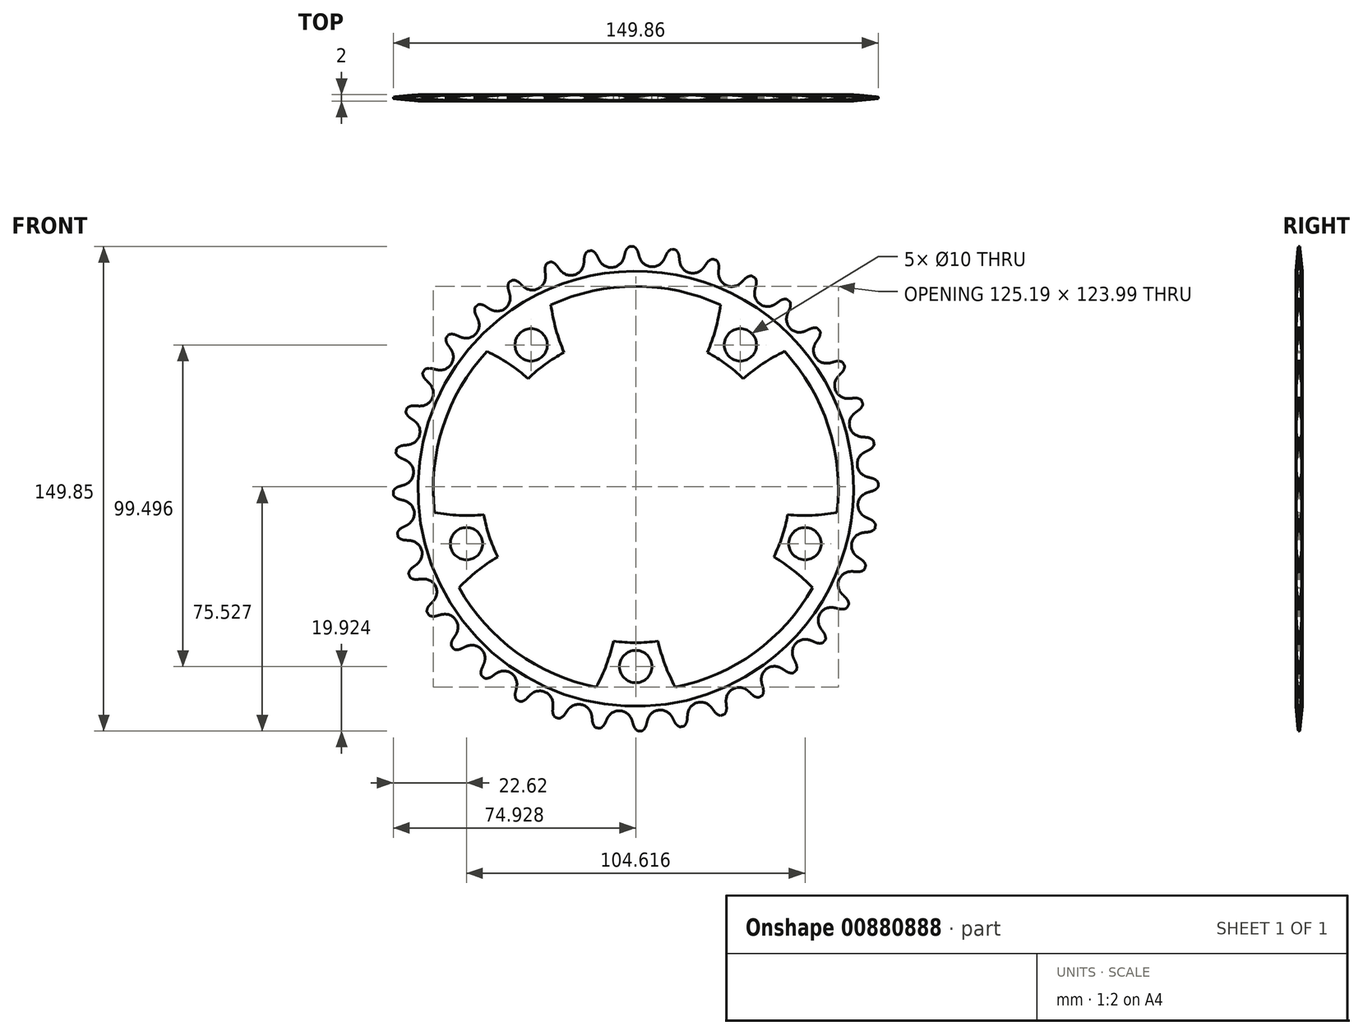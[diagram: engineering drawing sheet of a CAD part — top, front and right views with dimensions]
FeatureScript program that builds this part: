
annotation { "Feature Type Name" : "Feature", "Feature Type Description" : "" }
export const myFeature = defineFeature(function(context is Context, id is Id, definition is map)
    precondition{}
    {
        {
            var Q0;
            Q0=qCreatedBy(makeId("Front.planeOp"),FACE);
            var sketch = newSketch(context, id + "F0", { "sketchPlane" : qUnion([Q0])});
            skArc(sketch, "E0", {"start": v(-38.32, -39.45) * mm, "mid": v(52.3, 17) * mm, "end": v(-54.2, 9.39) * mm, "construction": true});
            skCircle(sketch, "E1", {"center": v(0, 55) * mm, "radius": 5 * mm});
            skCircle(sketch, "E2.1.0", {"center": v(-52.3, 17) * mm, "radius": 5 * mm});
            skCircle(sketch, "E2.2.0", {"center": v(-32.33, -44.5) * mm, "radius": 5 * mm});
            skCircle(sketch, "E2.3.0", {"center": v(32.33, -44.5) * mm, "radius": 5 * mm});
            skCircle(sketch, "E2.4.0", {"center": v(52.3, 17) * mm, "radius": 5 * mm});
            skLineSegment(sketch, "E3", {"start": v(0, 55) * mm, "end": v(0, 7.81) * mm, "construction": true});
            skLineSegment(sketch, "E4.2.3.0", {"start": v(21.9, -38.96) * mm, "end": v(21.9, -38.96) * mm});
            skLineSegment(sketch, "E4.4.3.0", {"start": v(32.98, -30.9) * mm, "end": v(32.98, -30.9) * mm});
            skLineSegment(sketch, "E5", {"start": v(41.79, 25.51) * mm, "end": v(41.79, 25.51) * mm});
            skArc(sketch, "E6", {"start": v(46.92, 8.04) * mm, "mid": v(45.27, 14.7) * mm, "end": v(42.68, 21.07) * mm});
            skArc(sketch, "E7", {"start": v(22.14, -42.14) * mm, "mid": v(27.98, -38.5) * mm, "end": v(33.23, -34.08) * mm});
            skArc(sketch, "E8", {"start": v(-33.23, -34.08) * mm, "mid": v(-27.98, -38.5) * mm, "end": v(-22.14, -42.14) * mm});
            skArc(sketch, "E9", {"start": v(-42.68, 21.07) * mm, "mid": v(-45.27, 14.7) * mm, "end": v(-46.92, 8.04) * mm});
            skArc(sketch, "E10.1.0", {"start": v(6.85, 47.1) * mm, "mid": v(0, 47.6) * mm, "end": v(-6.85, 47.1) * mm});
            skCircle(sketch, "E11", {"center": v(0, 0) * mm, "radius": 74.93 * mm});
            skPoint(sketch, "E12.orphan", {"position": v(26.2, -56.86) * mm});
            skPoint(sketch, "E13.orphan", {"position": v(45.98, -42.48) * mm});
            skPoint(sketch, "E14.orphan", {"position": v(-26.2, -56.86) * mm});
            skPoint(sketch, "E15.orphan", {"position": v(-45.98, -42.48) * mm});
            skPoint(sketch, "E16.orphan", {"position": v(-62.17, 7.34) * mm});
            skPoint(sketch, "E17.orphan", {"position": v(-54.61, 30.6) * mm});
            skPoint(sketch, "E18.orphan", {"position": v(-12.23, 61.4) * mm});
            skPoint(sketch, "E19.orphan", {"position": v(12.23, 61.4) * mm});
            skPoint(sketch, "E20.orphan", {"position": v(62.17, 7.34) * mm});
            skPoint(sketch, "E21.orphan", {"position": v(42.68, 21.07) * mm});
            skPoint(sketch, "E22.orphan", {"position": v(-22.14, -42.14) * mm});
            skPoint(sketch, "E23.orphan", {"position": v(-33.23, -34.08) * mm});
            skPoint(sketch, "E24.orphan", {"position": v(-46.92, 8.04) * mm});
            skPoint(sketch, "E25.MirrorCS.start.orphan", {"position": v(6.85, 47.1) * mm});
            skPoint(sketch, "E26.orphan", {"position": v(-6.85, 47.1) * mm});
            skArc(sketch, "E27", {"start": v(-54.61, 30.6) * mm, "mid": v(-48.97, 25.43) * mm, "end": v(-42.68, 21.07) * mm});
            skLineSegment(sketch, "E28.MirrorCS", {"start": v(-62.42, 10.52) * mm, "end": v(-62.42, 10.52) * mm});
            skArc(sketch, "E29.1.0", {"start": v(-45.98, -42.48) * mm, "mid": v(-39.32, -38.72) * mm, "end": v(-33.23, -34.08) * mm});
            skArc(sketch, "E29.1.1", {"start": v(-26.2, -56.86) * mm, "mid": v(-24.67, -49.36) * mm, "end": v(-22.14, -42.14) * mm});
            skArc(sketch, "E29.2.0", {"start": v(26.2, -56.86) * mm, "mid": v(24.67, -49.36) * mm, "end": v(22.14, -42.14) * mm});
            skLineSegment(sketch, "E29.2.1", {"start": v(45.73, -39.3) * mm, "end": v(45.73, -39.3) * mm});
            skArc(sketch, "E29.3.0", {"start": v(62.17, 7.34) * mm, "mid": v(54.57, 8.21) * mm, "end": v(46.92, 8.04) * mm});
            skArc(sketch, "E29.3.1", {"start": v(54.61, 30.6) * mm, "mid": v(48.97, 25.43) * mm, "end": v(42.68, 21.07) * mm});
            skArc(sketch, "E29.4.0", {"start": v(12.23, 61.4) * mm, "mid": v(9.05, 54.43) * mm, "end": v(6.85, 47.1) * mm});
            skArc(sketch, "E29.4.1", {"start": v(-12.23, 61.4) * mm, "mid": v(-9.05, 54.43) * mm, "end": v(-6.85, 47.1) * mm});
            skArc(sketch, "E30", {"start": v(-12.23, 61.4) * mm, "mid": v(-36.8, 50.64) * mm, "end": v(-54.61, 30.6) * mm});
            skArc(sketch, "E31", {"start": v(54.61, 30.6) * mm, "mid": v(36.8, 50.64) * mm, "end": v(12.23, 61.4) * mm});
            skArc(sketch, "E32", {"start": v(45.98, -42.48) * mm, "mid": v(39.32, -38.72) * mm, "end": v(33.23, -34.08) * mm});
            skArc(sketch, "E33", {"start": v(45.98, -42.48) * mm, "mid": v(59.54, -19.34) * mm, "end": v(62.17, 7.34) * mm});
            skArc(sketch, "E34", {"start": v(-62.17, 7.34) * mm, "mid": v(-59.54, -19.34) * mm, "end": v(-45.98, -42.48) * mm});
            skArc(sketch, "E35", {"start": v(-62.17, 7.34) * mm, "mid": v(-54.57, 8.21) * mm, "end": v(-46.92, 8.04) * mm});
            skArc(sketch, "E36", {"start": v(-26.2, -56.86) * mm, "mid": v(0, -62.6) * mm, "end": v(26.2, -56.86) * mm});
            skSolve(sketch);
        }
        {
            var Q0;
            Q0=qCreatedBy(makeId("Front.planeOp"),FACE);
            cPlane(context, id + "F1", {"entities" : qUnion([Q0]), "cplaneType" : CPlaneType.OFFSET, "offset" : 25.4 * mm, "width" : 152.4 * mm, "height" : 152.4 * mm});
        }
        {
            var Q0;
            Q0=qCreatedBy(id+"F1.planeOp",FACE);
            var sketch = newSketch(context, id + "F2", { "sketchPlane" : qUnion([Q0])});
            skCircle(sketch, "E37", {"center": v(0, 0) * mm, "radius": 72.86 * mm, "construction": true});
            skLineSegment(sketch, "E38", {"start": v(0, 0) * mm, "end": v(0, 72.86) * mm, "construction": true});
            skLineSegment(sketch, "E39", {"start": v(0, 72.86) * mm, "end": v(8.72, 72.86) * mm, "construction": true});
            skLineSegment(sketch, "E40", {"start": v(0, 72.86) * mm, "end": v(0.93, 73.55) * mm, "construction": true});
            skLineSegment(sketch, "E41", {"start": v(0.93, 73.55) * mm, "end": v(-3.94, 71.76) * mm, "construction": true});
            skLineSegment(sketch, "E42", {"start": v(-123.38, 117.03) * mm, "end": v(-123.38, 117.03) * mm});
            skLineSegment(sketch, "E43", {"start": v(-6.56, 75) * mm, "end": v(0, 0) * mm, "construction": true});
            skArc(sketch, "E44", {"start": v(-6.56, 75) * mm, "mid": v(-9.6, 69.52) * mm, "end": v(-4.4, 73) * mm, "construction": true});
            skArc(sketch, "E45", {"start": v(-4.4, 73) * mm, "mid": v(-5.24, 74.26) * mm, "end": v(-6.56, 75) * mm});
            skArc(sketch, "E46", {"start": v(-3.94, 71.76) * mm, "mid": v(-3.63, 71.08) * mm, "end": v(-3.23, 70.45) * mm});
            skLineSegment(sketch, "E47", {"start": v(-122.67, 115.72) * mm, "end": v(-122.67, 115.72) * mm});
            skLineSegment(sketch, "E48", {"start": v(-4.4, 73) * mm, "end": v(-5.3, 75.44) * mm, "construction": true});
            skLineSegment(sketch, "E49", {"start": v(-3.94, 71.76) * mm, "end": v(-4.4, 73) * mm});
            skArc(sketch, "E50.MirrorCS", {"start": v(4.4, 73) * mm, "mid": v(5.24, 74.26) * mm, "end": v(6.56, 75) * mm});
            skLineSegment(sketch, "E51.MirrorCS", {"start": v(3.94, 71.76) * mm, "end": v(4.4, 73) * mm});
            skArc(sketch, "E52.MirrorCS", {"start": v(3.94, 71.76) * mm, "mid": v(3.63, 71.08) * mm, "end": v(3.23, 70.45) * mm});
            skArc(sketch, "E53", {"start": v(-3.23, 70.45) * mm, "mid": v(5.5, 76.02) * mm, "end": v(-3.94, 71.76) * mm, "construction": true});
            skLineSegment(sketch, "E54", {"start": v(-116.21, 115.72) * mm, "end": v(-116.21, 115.72) * mm});
            skArc(sketch, "E55", {"start": v(-3.23, 70.45) * mm, "mid": v(0, 68.83) * mm, "end": v(3.23, 70.45) * mm});
            skArc(sketch, "E56", {"start": v(3.23, 70.45) * mm, "mid": v(0, 76.89) * mm, "end": v(-3.23, 70.45) * mm, "construction": true});
            skArc(sketch, "E57.1.0", {"start": v(-17, 71.13) * mm, "mid": v(-18.05, 72.22) * mm, "end": v(-19.48, 72.71) * mm});
            skLineSegment(sketch, "E57.1.1", {"start": v(-16.34, 69.98) * mm, "end": v(-17, 71.13) * mm});
            skArc(sketch, "E57.1.2", {"start": v(-16.34, 69.98) * mm, "mid": v(-15.92, 69.37) * mm, "end": v(-15.42, 68.82) * mm});
            skArc(sketch, "E57.1.3", {"start": v(-15.42, 68.82) * mm, "mid": v(-11.95, 67.79) * mm, "end": v(-9.05, 69.94) * mm});
            skArc(sketch, "E57.1.4", {"start": v(-8.58, 71.35) * mm, "mid": v(-8.77, 70.63) * mm, "end": v(-9.05, 69.94) * mm});
            skLineSegment(sketch, "E57.1.5", {"start": v(-8.58, 71.35) * mm, "end": v(-8.35, 72.66) * mm});
            skArc(sketch, "E57.1.6", {"start": v(-8.35, 72.66) * mm, "mid": v(-7.74, 74.04) * mm, "end": v(-6.56, 75) * mm});
            skArc(sketch, "E57.2.0", {"start": v(-29.1, 67.1) * mm, "mid": v(-30.32, 68) * mm, "end": v(-31.81, 68.23) * mm});
            skLineSegment(sketch, "E57.2.1", {"start": v(-28.24, 66.08) * mm, "end": v(-29.1, 67.1) * mm});
            skArc(sketch, "E57.2.2", {"start": v(-28.24, 66.08) * mm, "mid": v(-27.72, 65.55) * mm, "end": v(-27.13, 65.1) * mm});
            skArc(sketch, "E57.2.3", {"start": v(-27.13, 65.1) * mm, "mid": v(-23.54, 64.68) * mm, "end": v(-21.06, 67.3) * mm});
            skArc(sketch, "E57.2.4", {"start": v(-20.84, 68.78) * mm, "mid": v(-20.9, 68.04) * mm, "end": v(-21.06, 67.3) * mm});
            skLineSegment(sketch, "E57.2.5", {"start": v(-20.84, 68.78) * mm, "end": v(-20.84, 70.1) * mm});
            skArc(sketch, "E57.2.6", {"start": v(-20.84, 70.1) * mm, "mid": v(-20.48, 71.57) * mm, "end": v(-19.48, 72.71) * mm});
            skArc(sketch, "E57.3.0", {"start": v(-40.3, 61.02) * mm, "mid": v(-41.67, 61.7) * mm, "end": v(-43.18, 61.67) * mm});
            skLineSegment(sketch, "E57.3.1", {"start": v(-39.29, 60.18) * mm, "end": v(-40.3, 61.02) * mm});
            skArc(sketch, "E57.3.2", {"start": v(-39.29, 60.18) * mm, "mid": v(-38.68, 59.74) * mm, "end": v(-38.02, 59.4) * mm});
            skArc(sketch, "E57.3.3", {"start": v(-38.02, 59.4) * mm, "mid": v(-34.42, 59.6) * mm, "end": v(-32.43, 62.63) * mm});
            skArc(sketch, "E57.3.4", {"start": v(-32.47, 64.11) * mm, "mid": v(-32.4, 63.37) * mm, "end": v(-32.43, 62.63) * mm});
            skLineSegment(sketch, "E57.3.5", {"start": v(-32.47, 64.11) * mm, "end": v(-32.7, 65.42) * mm});
            skArc(sketch, "E57.3.6", {"start": v(-32.7, 65.42) * mm, "mid": v(-32.6, 66.93) * mm, "end": v(-31.81, 68.23) * mm});
            skArc(sketch, "E57.4.0", {"start": v(-50.3, 53.1) * mm, "mid": v(-51.75, 53.52) * mm, "end": v(-53.23, 53.23) * mm});
            skLineSegment(sketch, "E57.4.1", {"start": v(-49.14, 52.44) * mm, "end": v(-50.3, 53.1) * mm});
            skArc(sketch, "E57.4.2", {"start": v(-49.14, 52.44) * mm, "mid": v(-48.47, 52.12) * mm, "end": v(-47.76, 51.9) * mm});
            skArc(sketch, "E57.4.3", {"start": v(-47.76, 51.9) * mm, "mid": v(-44.24, 52.73) * mm, "end": v(-42.81, 56.05) * mm});
            skArc(sketch, "E57.4.4", {"start": v(-43.1, 57.5) * mm, "mid": v(-42.9, 56.78) * mm, "end": v(-42.81, 56.05) * mm});
            skLineSegment(sketch, "E57.4.5", {"start": v(-43.1, 57.5) * mm, "end": v(-43.56, 58.75) * mm});
            skArc(sketch, "E57.4.6", {"start": v(-43.56, 58.75) * mm, "mid": v(-43.72, 60.25) * mm, "end": v(-43.18, 61.67) * mm});
            skArc(sketch, "E57.5.0", {"start": v(-58.75, 43.56) * mm, "mid": v(-60.25, 43.72) * mm, "end": v(-61.67, 43.18) * mm});
            skLineSegment(sketch, "E57.5.1", {"start": v(-57.5, 43.1) * mm, "end": v(-58.75, 43.56) * mm});
            skArc(sketch, "E57.5.2", {"start": v(-57.5, 43.1) * mm, "mid": v(-56.78, 42.9) * mm, "end": v(-56.05, 42.81) * mm});
            skArc(sketch, "E57.5.3", {"start": v(-56.05, 42.81) * mm, "mid": v(-52.73, 44.24) * mm, "end": v(-51.9, 47.76) * mm});
            skArc(sketch, "E57.5.4", {"start": v(-52.44, 49.14) * mm, "mid": v(-52.12, 48.47) * mm, "end": v(-51.9, 47.76) * mm});
            skLineSegment(sketch, "E57.5.5", {"start": v(-52.44, 49.14) * mm, "end": v(-53.1, 50.3) * mm});
            skArc(sketch, "E57.5.6", {"start": v(-53.1, 50.3) * mm, "mid": v(-53.52, 51.75) * mm, "end": v(-53.23, 53.23) * mm});
            skArc(sketch, "E57.6.0", {"start": v(-65.42, 32.7) * mm, "mid": v(-66.93, 32.6) * mm, "end": v(-68.23, 31.81) * mm});
            skLineSegment(sketch, "E57.6.1", {"start": v(-64.11, 32.47) * mm, "end": v(-65.42, 32.7) * mm});
            skArc(sketch, "E57.6.2", {"start": v(-64.11, 32.47) * mm, "mid": v(-63.37, 32.4) * mm, "end": v(-62.63, 32.43) * mm});
            skArc(sketch, "E57.6.3", {"start": v(-62.63, 32.43) * mm, "mid": v(-59.6, 34.42) * mm, "end": v(-59.4, 38.02) * mm});
            skArc(sketch, "E57.6.4", {"start": v(-60.18, 39.29) * mm, "mid": v(-59.74, 38.68) * mm, "end": v(-59.4, 38.02) * mm});
            skLineSegment(sketch, "E57.6.5", {"start": v(-60.18, 39.29) * mm, "end": v(-61.02, 40.3) * mm});
            skArc(sketch, "E57.6.6", {"start": v(-61.02, 40.3) * mm, "mid": v(-61.7, 41.67) * mm, "end": v(-61.67, 43.18) * mm});
            skArc(sketch, "E57.7.0", {"start": v(-70.1, 20.84) * mm, "mid": v(-71.57, 20.48) * mm, "end": v(-72.71, 19.48) * mm});
            skLineSegment(sketch, "E57.7.1", {"start": v(-68.78, 20.84) * mm, "end": v(-70.1, 20.84) * mm});
            skArc(sketch, "E57.7.2", {"start": v(-68.78, 20.84) * mm, "mid": v(-68.04, 20.9) * mm, "end": v(-67.3, 21.06) * mm});
            skArc(sketch, "E57.7.3", {"start": v(-67.3, 21.06) * mm, "mid": v(-64.68, 23.54) * mm, "end": v(-65.1, 27.13) * mm});
            skArc(sketch, "E57.7.4", {"start": v(-66.08, 28.24) * mm, "mid": v(-65.55, 27.72) * mm, "end": v(-65.1, 27.13) * mm});
            skLineSegment(sketch, "E57.7.5", {"start": v(-66.08, 28.24) * mm, "end": v(-67.1, 29.1) * mm});
            skArc(sketch, "E57.7.6", {"start": v(-67.1, 29.1) * mm, "mid": v(-68, 30.32) * mm, "end": v(-68.23, 31.81) * mm});
            skArc(sketch, "E57.8.0", {"start": v(-72.66, 8.35) * mm, "mid": v(-74.04, 7.74) * mm, "end": v(-75, 6.56) * mm});
            skLineSegment(sketch, "E57.8.1", {"start": v(-71.35, 8.58) * mm, "end": v(-72.66, 8.35) * mm});
            skArc(sketch, "E57.8.2", {"start": v(-71.35, 8.58) * mm, "mid": v(-70.63, 8.77) * mm, "end": v(-69.94, 9.05) * mm});
            skArc(sketch, "E57.8.3", {"start": v(-69.94, 9.05) * mm, "mid": v(-67.79, 11.95) * mm, "end": v(-68.82, 15.42) * mm});
            skArc(sketch, "E57.8.4", {"start": v(-69.98, 16.34) * mm, "mid": v(-69.37, 15.92) * mm, "end": v(-68.82, 15.42) * mm});
            skLineSegment(sketch, "E57.8.5", {"start": v(-69.98, 16.34) * mm, "end": v(-71.13, 17) * mm});
            skArc(sketch, "E57.8.6", {"start": v(-71.13, 17) * mm, "mid": v(-72.22, 18.05) * mm, "end": v(-72.71, 19.48) * mm});
            skArc(sketch, "E57.9.0", {"start": v(-73, -4.4) * mm, "mid": v(-74.26, -5.24) * mm, "end": v(-75, -6.56) * mm});
            skLineSegment(sketch, "E57.9.1", {"start": v(-71.76, -3.94) * mm, "end": v(-73, -4.4) * mm});
            skArc(sketch, "E57.9.2", {"start": v(-71.76, -3.94) * mm, "mid": v(-71.08, -3.63) * mm, "end": v(-70.45, -3.23) * mm});
            skArc(sketch, "E57.9.3", {"start": v(-70.45, -3.23) * mm, "mid": v(-68.83, 0) * mm, "end": v(-70.45, 3.23) * mm});
            skArc(sketch, "E57.9.4", {"start": v(-71.76, 3.94) * mm, "mid": v(-71.08, 3.63) * mm, "end": v(-70.45, 3.23) * mm});
            skLineSegment(sketch, "E57.9.5", {"start": v(-71.76, 3.94) * mm, "end": v(-73, 4.4) * mm});
            skArc(sketch, "E57.9.6", {"start": v(-73, 4.4) * mm, "mid": v(-74.26, 5.24) * mm, "end": v(-75, 6.56) * mm});
            skArc(sketch, "E57.10.0", {"start": v(-71.13, -17) * mm, "mid": v(-72.22, -18.05) * mm, "end": v(-72.71, -19.48) * mm});
            skLineSegment(sketch, "E57.10.1", {"start": v(-69.98, -16.34) * mm, "end": v(-71.13, -17) * mm});
            skArc(sketch, "E57.10.2", {"start": v(-69.98, -16.34) * mm, "mid": v(-69.37, -15.92) * mm, "end": v(-68.82, -15.42) * mm});
            skArc(sketch, "E57.10.3", {"start": v(-68.82, -15.42) * mm, "mid": v(-67.79, -11.95) * mm, "end": v(-69.94, -9.05) * mm});
            skArc(sketch, "E57.10.4", {"start": v(-71.35, -8.58) * mm, "mid": v(-70.63, -8.77) * mm, "end": v(-69.94, -9.05) * mm});
            skLineSegment(sketch, "E57.10.5", {"start": v(-71.35, -8.58) * mm, "end": v(-72.66, -8.35) * mm});
            skArc(sketch, "E57.10.6", {"start": v(-72.66, -8.35) * mm, "mid": v(-74.04, -7.74) * mm, "end": v(-75, -6.56) * mm});
            skArc(sketch, "E57.11.0", {"start": v(-67.1, -29.1) * mm, "mid": v(-68, -30.32) * mm, "end": v(-68.23, -31.81) * mm});
            skLineSegment(sketch, "E57.11.1", {"start": v(-66.08, -28.24) * mm, "end": v(-67.1, -29.1) * mm});
            skArc(sketch, "E57.11.2", {"start": v(-66.08, -28.24) * mm, "mid": v(-65.55, -27.72) * mm, "end": v(-65.1, -27.13) * mm});
            skArc(sketch, "E57.11.3", {"start": v(-65.1, -27.13) * mm, "mid": v(-64.68, -23.54) * mm, "end": v(-67.3, -21.06) * mm});
            skArc(sketch, "E57.11.4", {"start": v(-68.78, -20.84) * mm, "mid": v(-68.04, -20.9) * mm, "end": v(-67.3, -21.06) * mm});
            skLineSegment(sketch, "E57.11.5", {"start": v(-68.78, -20.84) * mm, "end": v(-70.1, -20.84) * mm});
            skArc(sketch, "E57.11.6", {"start": v(-70.1, -20.84) * mm, "mid": v(-71.57, -20.48) * mm, "end": v(-72.71, -19.48) * mm});
            skArc(sketch, "E57.12.0", {"start": v(-61.02, -40.3) * mm, "mid": v(-61.7, -41.67) * mm, "end": v(-61.67, -43.18) * mm});
            skLineSegment(sketch, "E57.12.1", {"start": v(-60.18, -39.29) * mm, "end": v(-61.02, -40.3) * mm});
            skArc(sketch, "E57.12.2", {"start": v(-60.18, -39.29) * mm, "mid": v(-59.74, -38.68) * mm, "end": v(-59.4, -38.02) * mm});
            skArc(sketch, "E57.12.3", {"start": v(-59.4, -38.02) * mm, "mid": v(-59.6, -34.42) * mm, "end": v(-62.63, -32.43) * mm});
            skArc(sketch, "E57.12.4", {"start": v(-64.11, -32.47) * mm, "mid": v(-63.37, -32.4) * mm, "end": v(-62.63, -32.43) * mm});
            skLineSegment(sketch, "E57.12.5", {"start": v(-64.11, -32.47) * mm, "end": v(-65.42, -32.7) * mm});
            skArc(sketch, "E57.12.6", {"start": v(-65.42, -32.7) * mm, "mid": v(-66.93, -32.6) * mm, "end": v(-68.23, -31.81) * mm});
            skArc(sketch, "E57.13.0", {"start": v(-53.1, -50.3) * mm, "mid": v(-53.52, -51.75) * mm, "end": v(-53.23, -53.23) * mm});
            skLineSegment(sketch, "E57.13.1", {"start": v(-52.44, -49.14) * mm, "end": v(-53.1, -50.3) * mm});
            skArc(sketch, "E57.13.2", {"start": v(-52.44, -49.14) * mm, "mid": v(-52.12, -48.47) * mm, "end": v(-51.9, -47.76) * mm});
            skArc(sketch, "E57.13.3", {"start": v(-51.9, -47.76) * mm, "mid": v(-52.73, -44.24) * mm, "end": v(-56.05, -42.81) * mm});
            skArc(sketch, "E57.13.4", {"start": v(-57.5, -43.1) * mm, "mid": v(-56.78, -42.9) * mm, "end": v(-56.05, -42.81) * mm});
            skLineSegment(sketch, "E57.13.5", {"start": v(-57.5, -43.1) * mm, "end": v(-58.75, -43.56) * mm});
            skArc(sketch, "E57.13.6", {"start": v(-58.75, -43.56) * mm, "mid": v(-60.25, -43.72) * mm, "end": v(-61.67, -43.18) * mm});
            skArc(sketch, "E57.14.0", {"start": v(-43.56, -58.75) * mm, "mid": v(-43.72, -60.25) * mm, "end": v(-43.18, -61.67) * mm});
            skLineSegment(sketch, "E57.14.1", {"start": v(-43.1, -57.5) * mm, "end": v(-43.56, -58.75) * mm});
            skArc(sketch, "E57.14.2", {"start": v(-43.1, -57.5) * mm, "mid": v(-42.9, -56.78) * mm, "end": v(-42.81, -56.05) * mm});
            skArc(sketch, "E57.14.3", {"start": v(-42.81, -56.05) * mm, "mid": v(-44.24, -52.73) * mm, "end": v(-47.76, -51.9) * mm});
            skArc(sketch, "E57.14.4", {"start": v(-49.14, -52.44) * mm, "mid": v(-48.47, -52.12) * mm, "end": v(-47.76, -51.9) * mm});
            skLineSegment(sketch, "E57.14.5", {"start": v(-49.14, -52.44) * mm, "end": v(-50.3, -53.1) * mm});
            skArc(sketch, "E57.14.6", {"start": v(-50.3, -53.1) * mm, "mid": v(-51.75, -53.52) * mm, "end": v(-53.23, -53.23) * mm});
            skArc(sketch, "E57.15.0", {"start": v(-32.7, -65.42) * mm, "mid": v(-32.6, -66.93) * mm, "end": v(-31.81, -68.23) * mm});
            skLineSegment(sketch, "E57.15.1", {"start": v(-32.47, -64.11) * mm, "end": v(-32.7, -65.42) * mm});
            skArc(sketch, "E57.15.2", {"start": v(-32.47, -64.11) * mm, "mid": v(-32.4, -63.37) * mm, "end": v(-32.43, -62.63) * mm});
            skArc(sketch, "E57.15.3", {"start": v(-32.43, -62.63) * mm, "mid": v(-34.42, -59.6) * mm, "end": v(-38.02, -59.4) * mm});
            skArc(sketch, "E57.15.4", {"start": v(-39.29, -60.18) * mm, "mid": v(-38.68, -59.74) * mm, "end": v(-38.02, -59.4) * mm});
            skLineSegment(sketch, "E57.15.5", {"start": v(-39.29, -60.18) * mm, "end": v(-40.3, -61.02) * mm});
            skArc(sketch, "E57.15.6", {"start": v(-40.3, -61.02) * mm, "mid": v(-41.67, -61.7) * mm, "end": v(-43.18, -61.67) * mm});
            skArc(sketch, "E57.16.0", {"start": v(-20.84, -70.1) * mm, "mid": v(-20.48, -71.57) * mm, "end": v(-19.48, -72.71) * mm});
            skLineSegment(sketch, "E57.16.1", {"start": v(-20.84, -68.78) * mm, "end": v(-20.84, -70.1) * mm});
            skArc(sketch, "E57.16.2", {"start": v(-20.84, -68.78) * mm, "mid": v(-20.9, -68.04) * mm, "end": v(-21.06, -67.3) * mm});
            skArc(sketch, "E57.16.3", {"start": v(-21.06, -67.3) * mm, "mid": v(-23.54, -64.68) * mm, "end": v(-27.13, -65.1) * mm});
            skArc(sketch, "E57.16.4", {"start": v(-28.24, -66.08) * mm, "mid": v(-27.72, -65.55) * mm, "end": v(-27.13, -65.1) * mm});
            skLineSegment(sketch, "E57.16.5", {"start": v(-28.24, -66.08) * mm, "end": v(-29.1, -67.1) * mm});
            skArc(sketch, "E57.16.6", {"start": v(-29.1, -67.1) * mm, "mid": v(-30.32, -68) * mm, "end": v(-31.81, -68.23) * mm});
            skArc(sketch, "E57.17.0", {"start": v(-8.35, -72.66) * mm, "mid": v(-7.74, -74.04) * mm, "end": v(-6.56, -75) * mm});
            skLineSegment(sketch, "E57.17.1", {"start": v(-8.58, -71.35) * mm, "end": v(-8.35, -72.66) * mm});
            skArc(sketch, "E57.17.2", {"start": v(-8.58, -71.35) * mm, "mid": v(-8.77, -70.63) * mm, "end": v(-9.05, -69.94) * mm});
            skArc(sketch, "E57.17.3", {"start": v(-9.05, -69.94) * mm, "mid": v(-11.95, -67.79) * mm, "end": v(-15.42, -68.82) * mm});
            skArc(sketch, "E57.17.4", {"start": v(-16.34, -69.98) * mm, "mid": v(-15.92, -69.37) * mm, "end": v(-15.42, -68.82) * mm});
            skLineSegment(sketch, "E57.17.5", {"start": v(-16.34, -69.98) * mm, "end": v(-17, -71.13) * mm});
            skArc(sketch, "E57.17.6", {"start": v(-17, -71.13) * mm, "mid": v(-18.05, -72.22) * mm, "end": v(-19.48, -72.71) * mm});
            skArc(sketch, "E57.18.0", {"start": v(4.4, -73) * mm, "mid": v(5.24, -74.26) * mm, "end": v(6.56, -75) * mm});
            skLineSegment(sketch, "E57.18.1", {"start": v(3.94, -71.76) * mm, "end": v(4.4, -73) * mm});
            skArc(sketch, "E57.18.2", {"start": v(3.94, -71.76) * mm, "mid": v(3.63, -71.08) * mm, "end": v(3.23, -70.45) * mm});
            skArc(sketch, "E57.18.3", {"start": v(3.23, -70.45) * mm, "mid": v(0, -68.83) * mm, "end": v(-3.23, -70.45) * mm});
            skArc(sketch, "E57.18.4", {"start": v(-3.94, -71.76) * mm, "mid": v(-3.63, -71.08) * mm, "end": v(-3.23, -70.45) * mm});
            skLineSegment(sketch, "E57.18.5", {"start": v(-3.94, -71.76) * mm, "end": v(-4.4, -73) * mm});
            skArc(sketch, "E57.18.6", {"start": v(-4.4, -73) * mm, "mid": v(-5.24, -74.26) * mm, "end": v(-6.56, -75) * mm});
            skArc(sketch, "E57.19.0", {"start": v(17, -71.13) * mm, "mid": v(18.05, -72.22) * mm, "end": v(19.48, -72.71) * mm});
            skLineSegment(sketch, "E57.19.1", {"start": v(16.34, -69.98) * mm, "end": v(17, -71.13) * mm});
            skArc(sketch, "E57.19.2", {"start": v(16.34, -69.98) * mm, "mid": v(15.92, -69.37) * mm, "end": v(15.42, -68.82) * mm});
            skArc(sketch, "E57.19.3", {"start": v(15.42, -68.82) * mm, "mid": v(11.95, -67.79) * mm, "end": v(9.05, -69.94) * mm});
            skArc(sketch, "E57.19.4", {"start": v(8.58, -71.35) * mm, "mid": v(8.77, -70.63) * mm, "end": v(9.05, -69.94) * mm});
            skLineSegment(sketch, "E57.19.5", {"start": v(8.58, -71.35) * mm, "end": v(8.35, -72.66) * mm});
            skArc(sketch, "E57.19.6", {"start": v(8.35, -72.66) * mm, "mid": v(7.74, -74.04) * mm, "end": v(6.56, -75) * mm});
            skArc(sketch, "E57.20.0", {"start": v(29.1, -67.1) * mm, "mid": v(30.32, -68) * mm, "end": v(31.81, -68.23) * mm});
            skLineSegment(sketch, "E57.20.1", {"start": v(28.24, -66.08) * mm, "end": v(29.1, -67.1) * mm});
            skArc(sketch, "E57.20.2", {"start": v(28.24, -66.08) * mm, "mid": v(27.72, -65.55) * mm, "end": v(27.13, -65.1) * mm});
            skArc(sketch, "E57.20.3", {"start": v(27.13, -65.1) * mm, "mid": v(23.54, -64.68) * mm, "end": v(21.06, -67.3) * mm});
            skArc(sketch, "E57.20.4", {"start": v(20.84, -68.78) * mm, "mid": v(20.9, -68.04) * mm, "end": v(21.06, -67.3) * mm});
            skLineSegment(sketch, "E57.20.5", {"start": v(20.84, -68.78) * mm, "end": v(20.84, -70.1) * mm});
            skArc(sketch, "E57.20.6", {"start": v(20.84, -70.1) * mm, "mid": v(20.48, -71.57) * mm, "end": v(19.48, -72.71) * mm});
            skArc(sketch, "E57.21.0", {"start": v(40.3, -61.02) * mm, "mid": v(41.67, -61.7) * mm, "end": v(43.18, -61.67) * mm});
            skLineSegment(sketch, "E57.21.1", {"start": v(39.29, -60.18) * mm, "end": v(40.3, -61.02) * mm});
            skArc(sketch, "E57.21.2", {"start": v(39.29, -60.18) * mm, "mid": v(38.68, -59.74) * mm, "end": v(38.02, -59.4) * mm});
            skArc(sketch, "E57.21.3", {"start": v(38.02, -59.4) * mm, "mid": v(34.42, -59.6) * mm, "end": v(32.43, -62.63) * mm});
            skArc(sketch, "E57.21.4", {"start": v(32.47, -64.11) * mm, "mid": v(32.4, -63.37) * mm, "end": v(32.43, -62.63) * mm});
            skLineSegment(sketch, "E57.21.5", {"start": v(32.47, -64.11) * mm, "end": v(32.7, -65.42) * mm});
            skArc(sketch, "E57.21.6", {"start": v(32.7, -65.42) * mm, "mid": v(32.6, -66.93) * mm, "end": v(31.81, -68.23) * mm});
            skArc(sketch, "E57.22.0", {"start": v(50.3, -53.1) * mm, "mid": v(51.75, -53.52) * mm, "end": v(53.23, -53.23) * mm});
            skLineSegment(sketch, "E57.22.1", {"start": v(49.14, -52.44) * mm, "end": v(50.3, -53.1) * mm});
            skArc(sketch, "E57.22.2", {"start": v(49.14, -52.44) * mm, "mid": v(48.47, -52.12) * mm, "end": v(47.76, -51.9) * mm});
            skArc(sketch, "E57.22.3", {"start": v(47.76, -51.9) * mm, "mid": v(44.24, -52.73) * mm, "end": v(42.81, -56.05) * mm});
            skArc(sketch, "E57.22.4", {"start": v(43.1, -57.5) * mm, "mid": v(42.9, -56.78) * mm, "end": v(42.81, -56.05) * mm});
            skLineSegment(sketch, "E57.22.5", {"start": v(43.1, -57.5) * mm, "end": v(43.56, -58.75) * mm});
            skArc(sketch, "E57.22.6", {"start": v(43.56, -58.75) * mm, "mid": v(43.72, -60.25) * mm, "end": v(43.18, -61.67) * mm});
            skArc(sketch, "E57.23.0", {"start": v(58.75, -43.56) * mm, "mid": v(60.25, -43.72) * mm, "end": v(61.67, -43.18) * mm});
            skLineSegment(sketch, "E57.23.1", {"start": v(57.5, -43.1) * mm, "end": v(58.75, -43.56) * mm});
            skArc(sketch, "E57.23.2", {"start": v(57.5, -43.1) * mm, "mid": v(56.78, -42.9) * mm, "end": v(56.05, -42.81) * mm});
            skArc(sketch, "E57.23.3", {"start": v(56.05, -42.81) * mm, "mid": v(52.73, -44.24) * mm, "end": v(51.9, -47.76) * mm});
            skArc(sketch, "E57.23.4", {"start": v(52.44, -49.14) * mm, "mid": v(52.12, -48.47) * mm, "end": v(51.9, -47.76) * mm});
            skLineSegment(sketch, "E57.23.5", {"start": v(52.44, -49.14) * mm, "end": v(53.1, -50.3) * mm});
            skArc(sketch, "E57.23.6", {"start": v(53.1, -50.3) * mm, "mid": v(53.52, -51.75) * mm, "end": v(53.23, -53.23) * mm});
            skArc(sketch, "E57.24.0", {"start": v(65.42, -32.7) * mm, "mid": v(66.93, -32.6) * mm, "end": v(68.23, -31.81) * mm});
            skLineSegment(sketch, "E57.24.1", {"start": v(64.11, -32.47) * mm, "end": v(65.42, -32.7) * mm});
            skArc(sketch, "E57.24.2", {"start": v(64.11, -32.47) * mm, "mid": v(63.37, -32.4) * mm, "end": v(62.63, -32.43) * mm});
            skArc(sketch, "E57.24.3", {"start": v(62.63, -32.43) * mm, "mid": v(59.6, -34.42) * mm, "end": v(59.4, -38.02) * mm});
            skArc(sketch, "E57.24.4", {"start": v(60.18, -39.29) * mm, "mid": v(59.74, -38.68) * mm, "end": v(59.4, -38.02) * mm});
            skLineSegment(sketch, "E57.24.5", {"start": v(60.18, -39.29) * mm, "end": v(61.02, -40.3) * mm});
            skArc(sketch, "E57.24.6", {"start": v(61.02, -40.3) * mm, "mid": v(61.7, -41.67) * mm, "end": v(61.67, -43.18) * mm});
            skArc(sketch, "E57.25.0", {"start": v(70.1, -20.84) * mm, "mid": v(71.57, -20.48) * mm, "end": v(72.71, -19.48) * mm});
            skLineSegment(sketch, "E57.25.1", {"start": v(68.78, -20.84) * mm, "end": v(70.1, -20.84) * mm});
            skArc(sketch, "E57.25.2", {"start": v(68.78, -20.84) * mm, "mid": v(68.04, -20.9) * mm, "end": v(67.3, -21.06) * mm});
            skArc(sketch, "E57.25.3", {"start": v(67.3, -21.06) * mm, "mid": v(64.68, -23.54) * mm, "end": v(65.1, -27.13) * mm});
            skArc(sketch, "E57.25.4", {"start": v(66.08, -28.24) * mm, "mid": v(65.55, -27.72) * mm, "end": v(65.1, -27.13) * mm});
            skLineSegment(sketch, "E57.25.5", {"start": v(66.08, -28.24) * mm, "end": v(67.1, -29.1) * mm});
            skArc(sketch, "E57.25.6", {"start": v(67.1, -29.1) * mm, "mid": v(68, -30.32) * mm, "end": v(68.23, -31.81) * mm});
            skArc(sketch, "E57.26.0", {"start": v(72.66, -8.35) * mm, "mid": v(74.04, -7.74) * mm, "end": v(75, -6.56) * mm});
            skLineSegment(sketch, "E57.26.1", {"start": v(71.35, -8.58) * mm, "end": v(72.66, -8.35) * mm});
            skArc(sketch, "E57.26.2", {"start": v(71.35, -8.58) * mm, "mid": v(70.63, -8.77) * mm, "end": v(69.94, -9.05) * mm});
            skArc(sketch, "E57.26.3", {"start": v(69.94, -9.05) * mm, "mid": v(67.79, -11.95) * mm, "end": v(68.82, -15.42) * mm});
            skArc(sketch, "E57.26.4", {"start": v(69.98, -16.34) * mm, "mid": v(69.37, -15.92) * mm, "end": v(68.82, -15.42) * mm});
            skLineSegment(sketch, "E57.26.5", {"start": v(69.98, -16.34) * mm, "end": v(71.13, -17) * mm});
            skArc(sketch, "E57.26.6", {"start": v(71.13, -17) * mm, "mid": v(72.22, -18.05) * mm, "end": v(72.71, -19.48) * mm});
            skArc(sketch, "E57.27.0", {"start": v(73, 4.4) * mm, "mid": v(74.26, 5.24) * mm, "end": v(75, 6.56) * mm});
            skLineSegment(sketch, "E57.27.1", {"start": v(71.76, 3.94) * mm, "end": v(73, 4.4) * mm});
            skArc(sketch, "E57.27.2", {"start": v(71.76, 3.94) * mm, "mid": v(71.08, 3.63) * mm, "end": v(70.45, 3.23) * mm});
            skArc(sketch, "E57.27.3", {"start": v(70.45, 3.23) * mm, "mid": v(68.83, 0) * mm, "end": v(70.45, -3.23) * mm});
            skArc(sketch, "E57.27.4", {"start": v(71.76, -3.94) * mm, "mid": v(71.08, -3.63) * mm, "end": v(70.45, -3.23) * mm});
            skLineSegment(sketch, "E57.27.5", {"start": v(71.76, -3.94) * mm, "end": v(73, -4.4) * mm});
            skArc(sketch, "E57.27.6", {"start": v(73, -4.4) * mm, "mid": v(74.26, -5.24) * mm, "end": v(75, -6.56) * mm});
            skArc(sketch, "E57.28.0", {"start": v(71.13, 17) * mm, "mid": v(72.22, 18.05) * mm, "end": v(72.71, 19.48) * mm});
            skLineSegment(sketch, "E57.28.1", {"start": v(69.98, 16.34) * mm, "end": v(71.13, 17) * mm});
            skArc(sketch, "E57.28.2", {"start": v(69.98, 16.34) * mm, "mid": v(69.37, 15.92) * mm, "end": v(68.82, 15.42) * mm});
            skArc(sketch, "E57.28.3", {"start": v(68.82, 15.42) * mm, "mid": v(67.79, 11.95) * mm, "end": v(69.94, 9.05) * mm});
            skArc(sketch, "E57.28.4", {"start": v(71.35, 8.58) * mm, "mid": v(70.63, 8.77) * mm, "end": v(69.94, 9.05) * mm});
            skLineSegment(sketch, "E57.28.5", {"start": v(71.35, 8.58) * mm, "end": v(72.66, 8.35) * mm});
            skArc(sketch, "E57.28.6", {"start": v(72.66, 8.35) * mm, "mid": v(74.04, 7.74) * mm, "end": v(75, 6.56) * mm});
            skArc(sketch, "E57.29.0", {"start": v(67.1, 29.1) * mm, "mid": v(68, 30.32) * mm, "end": v(68.23, 31.81) * mm});
            skLineSegment(sketch, "E57.29.1", {"start": v(66.08, 28.24) * mm, "end": v(67.1, 29.1) * mm});
            skArc(sketch, "E57.29.2", {"start": v(66.08, 28.24) * mm, "mid": v(65.55, 27.72) * mm, "end": v(65.1, 27.13) * mm});
            skArc(sketch, "E57.29.3", {"start": v(65.1, 27.13) * mm, "mid": v(64.68, 23.54) * mm, "end": v(67.3, 21.06) * mm});
            skArc(sketch, "E57.29.4", {"start": v(68.78, 20.84) * mm, "mid": v(68.04, 20.9) * mm, "end": v(67.3, 21.06) * mm});
            skLineSegment(sketch, "E57.29.5", {"start": v(68.78, 20.84) * mm, "end": v(70.1, 20.84) * mm});
            skArc(sketch, "E57.29.6", {"start": v(70.1, 20.84) * mm, "mid": v(71.57, 20.48) * mm, "end": v(72.71, 19.48) * mm});
            skArc(sketch, "E57.30.0", {"start": v(61.02, 40.3) * mm, "mid": v(61.7, 41.67) * mm, "end": v(61.67, 43.18) * mm});
            skLineSegment(sketch, "E57.30.1", {"start": v(60.18, 39.29) * mm, "end": v(61.02, 40.3) * mm});
            skArc(sketch, "E57.30.2", {"start": v(60.18, 39.29) * mm, "mid": v(59.74, 38.68) * mm, "end": v(59.4, 38.02) * mm});
            skArc(sketch, "E57.30.3", {"start": v(59.4, 38.02) * mm, "mid": v(59.6, 34.42) * mm, "end": v(62.63, 32.43) * mm});
            skArc(sketch, "E57.30.4", {"start": v(64.11, 32.47) * mm, "mid": v(63.37, 32.4) * mm, "end": v(62.63, 32.43) * mm});
            skLineSegment(sketch, "E57.30.5", {"start": v(64.11, 32.47) * mm, "end": v(65.42, 32.7) * mm});
            skArc(sketch, "E57.30.6", {"start": v(65.42, 32.7) * mm, "mid": v(66.93, 32.6) * mm, "end": v(68.23, 31.81) * mm});
            skArc(sketch, "E57.31.0", {"start": v(53.1, 50.3) * mm, "mid": v(53.52, 51.75) * mm, "end": v(53.23, 53.23) * mm});
            skLineSegment(sketch, "E57.31.1", {"start": v(52.44, 49.14) * mm, "end": v(53.1, 50.3) * mm});
            skArc(sketch, "E57.31.2", {"start": v(52.44, 49.14) * mm, "mid": v(52.12, 48.47) * mm, "end": v(51.9, 47.76) * mm});
            skArc(sketch, "E57.31.3", {"start": v(51.9, 47.76) * mm, "mid": v(52.73, 44.24) * mm, "end": v(56.05, 42.81) * mm});
            skArc(sketch, "E57.31.4", {"start": v(57.5, 43.1) * mm, "mid": v(56.78, 42.9) * mm, "end": v(56.05, 42.81) * mm});
            skLineSegment(sketch, "E57.31.5", {"start": v(57.5, 43.1) * mm, "end": v(58.75, 43.56) * mm});
            skArc(sketch, "E57.31.6", {"start": v(58.75, 43.56) * mm, "mid": v(60.25, 43.72) * mm, "end": v(61.67, 43.18) * mm});
            skArc(sketch, "E57.32.0", {"start": v(43.56, 58.75) * mm, "mid": v(43.72, 60.25) * mm, "end": v(43.18, 61.67) * mm});
            skLineSegment(sketch, "E57.32.1", {"start": v(43.1, 57.5) * mm, "end": v(43.56, 58.75) * mm});
            skArc(sketch, "E57.32.2", {"start": v(43.1, 57.5) * mm, "mid": v(42.9, 56.78) * mm, "end": v(42.81, 56.05) * mm});
            skArc(sketch, "E57.32.3", {"start": v(42.81, 56.05) * mm, "mid": v(44.24, 52.73) * mm, "end": v(47.76, 51.9) * mm});
            skArc(sketch, "E57.32.4", {"start": v(49.14, 52.44) * mm, "mid": v(48.47, 52.12) * mm, "end": v(47.76, 51.9) * mm});
            skLineSegment(sketch, "E57.32.5", {"start": v(49.14, 52.44) * mm, "end": v(50.3, 53.1) * mm});
            skArc(sketch, "E57.32.6", {"start": v(50.3, 53.1) * mm, "mid": v(51.75, 53.52) * mm, "end": v(53.23, 53.23) * mm});
            skArc(sketch, "E57.33.0", {"start": v(32.7, 65.42) * mm, "mid": v(32.6, 66.93) * mm, "end": v(31.81, 68.23) * mm});
            skLineSegment(sketch, "E57.33.1", {"start": v(32.47, 64.11) * mm, "end": v(32.7, 65.42) * mm});
            skArc(sketch, "E57.33.2", {"start": v(32.47, 64.11) * mm, "mid": v(32.4, 63.37) * mm, "end": v(32.43, 62.63) * mm});
            skArc(sketch, "E57.33.3", {"start": v(32.43, 62.63) * mm, "mid": v(34.42, 59.6) * mm, "end": v(38.02, 59.4) * mm});
            skArc(sketch, "E57.33.4", {"start": v(39.29, 60.18) * mm, "mid": v(38.68, 59.74) * mm, "end": v(38.02, 59.4) * mm});
            skLineSegment(sketch, "E57.33.5", {"start": v(39.29, 60.18) * mm, "end": v(40.3, 61.02) * mm});
            skArc(sketch, "E57.33.6", {"start": v(40.3, 61.02) * mm, "mid": v(41.67, 61.7) * mm, "end": v(43.18, 61.67) * mm});
            skArc(sketch, "E57.34.0", {"start": v(20.84, 70.1) * mm, "mid": v(20.48, 71.57) * mm, "end": v(19.48, 72.71) * mm});
            skLineSegment(sketch, "E57.34.1", {"start": v(20.84, 68.78) * mm, "end": v(20.84, 70.1) * mm});
            skArc(sketch, "E57.34.2", {"start": v(20.84, 68.78) * mm, "mid": v(20.9, 68.04) * mm, "end": v(21.06, 67.3) * mm});
            skArc(sketch, "E57.34.3", {"start": v(21.06, 67.3) * mm, "mid": v(23.54, 64.68) * mm, "end": v(27.13, 65.1) * mm});
            skArc(sketch, "E57.34.4", {"start": v(28.24, 66.08) * mm, "mid": v(27.72, 65.55) * mm, "end": v(27.13, 65.1) * mm});
            skLineSegment(sketch, "E57.34.5", {"start": v(28.24, 66.08) * mm, "end": v(29.1, 67.1) * mm});
            skArc(sketch, "E57.34.6", {"start": v(29.1, 67.1) * mm, "mid": v(30.32, 68) * mm, "end": v(31.81, 68.23) * mm});
            skArc(sketch, "E57.35.0", {"start": v(8.35, 72.66) * mm, "mid": v(7.74, 74.04) * mm, "end": v(6.56, 75) * mm});
            skLineSegment(sketch, "E57.35.1", {"start": v(8.58, 71.35) * mm, "end": v(8.35, 72.66) * mm});
            skArc(sketch, "E57.35.2", {"start": v(8.58, 71.35) * mm, "mid": v(8.77, 70.63) * mm, "end": v(9.05, 69.94) * mm});
            skArc(sketch, "E57.35.3", {"start": v(9.05, 69.94) * mm, "mid": v(11.95, 67.79) * mm, "end": v(15.42, 68.82) * mm});
            skArc(sketch, "E57.35.4", {"start": v(16.34, 69.98) * mm, "mid": v(15.92, 69.37) * mm, "end": v(15.42, 68.82) * mm});
            skLineSegment(sketch, "E57.35.5", {"start": v(16.34, 69.98) * mm, "end": v(17, 71.13) * mm});
            skArc(sketch, "E57.35.6", {"start": v(17, 71.13) * mm, "mid": v(18.05, 72.22) * mm, "end": v(19.48, 72.71) * mm});
            skSolve(sketch);
        }
        {
            var Q0;
            Q0=makeQuery(id+"F0.imprint","IMPRINT",FACE,{"disambiguationData":[TD([[makeQuery(id+"F0.imprint","IMPRINT",EDGE,{"derivedFrom":sQuery(id+"F0.wireOp",EDGE,"E1")}),-1.0]])]});
            extrude(context, id + "F3", {"entities" : qUnion([Q0]), "depth" : 2 * mm, "offsetDistance" : 25.4 * mm});
        }
        {
            var Q0;
            Q0=makeQuery(id+"F3.opExtrude","CAP_EDGE",EDGE,{"disambiguationData":[OSD([sQuery(id+"F0.wireOp",EDGE,"E11")])],"isStart":true});
            var Q1;
            Q1=makeQuery(id+"F3.opExtrude","CAP_EDGE",EDGE,{"disambiguationData":[OSD([sQuery(id+"F0.wireOp",EDGE,"E11")])],"isStart":false});
            chamfer(context, id + "F4", {"entities" : qUnion([Q0, Q1]), "chamferType" : ChamferType.TWO_OFFSETS, "width1" : 0.76 * mm, "oppositeDirection" : false, "width2" : 7.62 * mm, "tangentPropagation" : true});
        }
        {
            var Q0;
            Q0 = qSketchRegion(id + "F2", true);
            extrude(context, id + "F5", {"entities" : qUnion([Q0]), "operationType" : NewBodyOperationType.INTERSECT, "oppositeDirection" : true, "depth" : 38.1 * mm, "offsetDistance" : 25.4 * mm});
        }
        {
            var Q0;
            Q0=makeQuery(id+"F3.opExtrude","SWEPT_BODY",BODY,{"disambiguationData":[OSD([sQuery(id+"F0.wireOp",EDGE,"E1"),sQuery(id+"F0.wireOp",EDGE,"E2.1.0"),sQuery(id+"F0.wireOp",EDGE,"E2.2.0"),sQuery(id+"F0.wireOp",EDGE,"E2.3.0"),sQuery(id+"F0.wireOp",EDGE,"E2.4.0"),sQuery(id+"F0.wireOp",EDGE,"E6"),sQuery(id+"F0.wireOp",EDGE,"E10.1.0"),sQuery(id+"F0.wireOp",EDGE,"E9"),sQuery(id+"F0.wireOp",EDGE,"E8"),sQuery(id+"F0.wireOp",EDGE,"E7"),sQuery(id+"F0.wireOp",EDGE,"E11"),sQuery(id+"F0.wireOp",EDGE,"E27"),sQuery(id+"F0.wireOp",EDGE,"E29.1.0"),sQuery(id+"F0.wireOp",EDGE,"E29.1.1"),sQuery(id+"F0.wireOp",EDGE,"E29.2.0"),sQuery(id+"F0.wireOp",EDGE,"E29.3.0"),sQuery(id+"F0.wireOp",EDGE,"E29.3.1"),sQuery(id+"F0.wireOp",EDGE,"E29.4.0"),sQuery(id+"F0.wireOp",EDGE,"E29.4.1"),sQuery(id+"F0.wireOp",EDGE,"E30"),sQuery(id+"F0.wireOp",EDGE,"E31"),sQuery(id+"F0.wireOp",EDGE,"E32"),sQuery(id+"F0.wireOp",EDGE,"E33"),sQuery(id+"F0.wireOp",EDGE,"E34"),sQuery(id+"F0.wireOp",EDGE,"E35"),sQuery(id+"F0.wireOp",EDGE,"E36")])]});
            var Q1;
            Q1=makeQuery(id+"F3.opExtrude","CAP_EDGE",EDGE,{"disambiguationData":[OSD([sQuery(id+"F0.wireOp",EDGE,"E1")])],"isStart":true});
            transform(context, id + "F6", {"entities" : qUnion([Q0]), "transformType" : TransformType.ROTATION, "transformAxis" : qUnion([Q1]), "angle" : 36 * degree, "makeCopy" : false});
        }
    });
